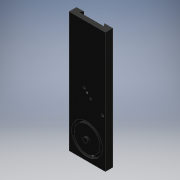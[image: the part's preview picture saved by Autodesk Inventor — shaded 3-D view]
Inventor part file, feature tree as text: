
AUTODESK INVENTOR PART (.ipt)
format: ipt  version: 2016 (Build 200138000, 138)  size: 217,088 bytes
history: native  units: mm
features: extrude x7, sketch x6, hole x3, thread x1
ambient origin geometry x8: Origin, YZ Plane, XZ Plane, XY Plane, X Axis, Y Axis, Z Axis, Center Point
bodies: Solid1 (feature_tree)
feature tree (17):
  extrude  "Extrusion1"  Depth=29.6mm
  sketch  "Sketch2"  dims[d2=29.9mm d4=22.68928mm]
  sketch  "Sketch3"  dims[d5=33.0mm d6=8.726646mm]
  extrude  "Extrusion2"  Depth=22.68928mm
  extrude  "Extrusion3"  Depth=8.726646mm
  extrude  "Extrusion4"  Depth=486.0mm
  sketch  "Sketch4"  dims[d7=486.0mm d8=0.0mm d9=22.0mm]
  extrude  "Extrusion5"  Depth=14.5mm
  extrude  "Extrusion7"  Depth=10.0mm
  extrude  "Extrusion8"  Depth=10.0mm
  sketch  "Sketch5"  dims[d10=124.2mm d11=14.5mm]
  sketch  "Sketch6"  dims[d12=62.1mm d13=104.0mm d14=19.02mm d15=8.2mm d17=13.0mm d18=0.0mm d19=7.5mm d20=0.0mm d21=7.5mm d22=0.0mm d23=19.0mm d24=3.7mm d25=0.0mm d26=9.4mm d29=0.0mm d30=18.7mm d31=18.7mm d36=6.0mm d37=0.0mm d38=17.0mm d39=46.5mm d40=3.0mm d41=0.0mm d42=10.0mm d43=225.0mm d44=60.0mm d45=11.0mm d46=60.5mm d47=250.5mm d48=11.0mm d49=190.5mm d50=11.5mm d51=8.5mm d52=6.0mm d53=11.0mm d54=8.5mm d55=90.0deg d56=8.0mm d57=20.594885mm d58=7.0mm d59=6.0mm d60=10.0mm d61=7.5mm d62=90.0deg d63=8.0mm d64=20.594885mm d65=7.5mm d66=6.0mm d67=11.0mm d68=7.0mm d69=90.0deg d70=8.0mm d71=20.594885mm d75=10.0mm d76=0.0mm]
  hole  "Hole1"  [1 undecoded]
  hole  "Hole2"  [1 undecoded]
  hole  "Hole3"  [1 undecoded]
  thread  "Thread1"  [1 undecoded]
  sketch  "Sketch1"  dims[d0=146.0mm d1=29.6mm]
note: 4 required parameter values undecoded (feature->parameter linkage not recoverable at this tier; creation-order binding heuristic only, values carry confidence <= 0.55)
